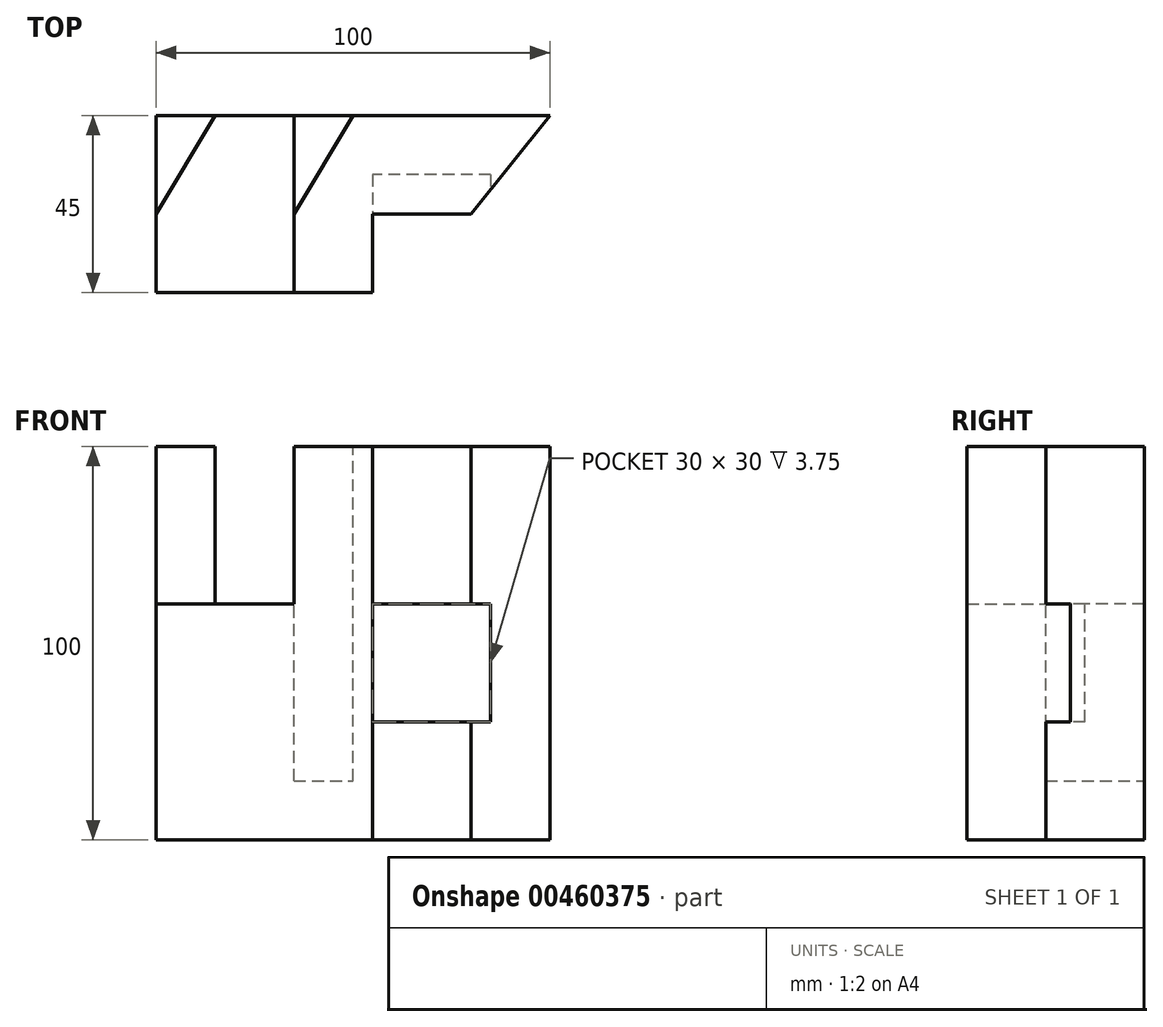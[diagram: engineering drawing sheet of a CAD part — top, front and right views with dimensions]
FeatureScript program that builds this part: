
annotation { "Feature Type Name" : "Feature", "Feature Type Description" : "" }
export const myFeature = defineFeature(function(context is Context, id is Id, definition is map)
    precondition{}
    {
        {
            var Q0;
            Q0=qCreatedBy(makeId("Front.planeOp"),FACE);
            var sketch = newSketch(context, id + "F0", { "sketchPlane" : qUnion([Q0])});
            skLineSegment(sketch, "E0.bottom", {"start": v(0, 0) * mm, "end": v(100, 0) * mm});
            skLineSegment(sketch, "E0.top", {"start": v(0, 100) * mm, "end": v(100, 100) * mm});
            skLineSegment(sketch, "E0.left", {"start": v(0, 0) * mm, "end": v(0, 100) * mm});
            skLineSegment(sketch, "E0.right", {"start": v(100, 0) * mm, "end": v(100, 100) * mm});
            skSolve(sketch);
        }
        {
            var Q0;
            Q0=makeQuery(id+"F0.imprint","IMPRINT",FACE,{"disambiguationData":[TD([[makeQuery(id+"F0.imprint","IMPRINT",EDGE,{"derivedFrom":sQuery(id+"F0.wireOp",EDGE,"E0.bottom")}),1.0]])]});
            extrude(context, id + "F1", {"entities" : qUnion([Q0]), "depth" : 45 * mm});
        }
        {
            var Q0;
            Q0=makeQuery(id+"F1.opExtrude","CAP_FACE",FACE,{"disambiguationData":[OSD([sQuery(id+"F0.wireOp",EDGE,"E0.bottom"),sQuery(id+"F0.wireOp",EDGE,"E0.top"),sQuery(id+"F0.wireOp",EDGE,"E0.left"),sQuery(id+"F0.wireOp",EDGE,"E0.right")])],"isStart":false});
            var sketch = newSketch(context, id + "F2", { "sketchPlane" : qUnion([Q0])});
            skLineSegment(sketch, "E1.bottom", {"start": v(100, 0) * mm, "end": v(55, 0) * mm});
            skLineSegment(sketch, "E1.top", {"start": v(100, 100) * mm, "end": v(55, 100) * mm});
            skLineSegment(sketch, "E1.left", {"start": v(100, 0) * mm, "end": v(100, 100) * mm});
            skLineSegment(sketch, "E1.right", {"start": v(55, 0) * mm, "end": v(55, 100) * mm});
            skSolve(sketch);
        }
        {
            var Q0;
            Q0=makeQuery(id+"F2.imprint","IMPRINT",FACE,{"disambiguationData":[TD([[makeQuery(id+"F2.imprint","IMPRINT",EDGE,{"derivedFrom":sQuery(id+"F2.wireOp",EDGE,"E1.bottom")}),1.0]])]});
            extrude(context, id + "F3", {"entities" : qUnion([Q0]), "operationType" : NewBodyOperationType.REMOVE, "oppositeDirection" : true, "depth" : 20 * mm});
        }
        {
            var Q0;
            Q0=makeQuery(id+"F1.opExtrude","SWEPT_FACE",FACE,{"disambiguationData":[OSD([sQuery(id+"F0.wireOp",EDGE,"E0.top")])]});
            var sketch = newSketch(context, id + "F4", { "sketchPlane" : qUnion([Q0])});
            skLineSegment(sketch, "E2.bottom", {"start": v(0, -45) * mm, "end": v(35, -45) * mm});
            skLineSegment(sketch, "E2.top", {"start": v(0, 0) * mm, "end": v(35, 0) * mm});
            skLineSegment(sketch, "E2.left", {"start": v(0, -45) * mm, "end": v(0, 0) * mm});
            skLineSegment(sketch, "E2.right", {"start": v(35, -45) * mm, "end": v(35, 0) * mm});
            skSolve(sketch);
        }
        {
            var Q0;
            Q0=makeQuery(id+"F4.imprint","IMPRINT",FACE,{"disambiguationData":[TD([[makeQuery(id+"F4.imprint","IMPRINT",EDGE,{"derivedFrom":sQuery(id+"F4.wireOp",EDGE,"E2.bottom")}),1.0]])]});
            extrude(context, id + "F5", {"entities" : qUnion([Q0]), "operationType" : NewBodyOperationType.REMOVE, "oppositeDirection" : true, "depth" : 40 * mm});
        }
        {
            var Q0;
            Q0=makeQuery(id+"F5.boolean.opBoolean","COPY",FACE,{"derivedFrom":makeQuery(id+"F5.opExtrude","CAP_FACE",FACE,{"disambiguationData":[OSD([sQuery(id+"F4.wireOp",EDGE,"E2.bottom"),sQuery(id+"F4.wireOp",EDGE,"E2.top"),sQuery(id+"F4.wireOp",EDGE,"E2.left"),sQuery(id+"F4.wireOp",EDGE,"E2.right")])],"isStart":false})});
            var sketch = newSketch(context, id + "F6", { "sketchPlane" : qUnion([Q0])});
            skLineSegment(sketch, "E3", {"start": v(0, 0) * mm, "end": v(15, 0) * mm});
            skLineSegment(sketch, "E4", {"start": v(15, 0) * mm, "end": v(0, -25) * mm});
            skLineSegment(sketch, "E5", {"start": v(0, -25) * mm, "end": v(0, 0) * mm});
            skSolve(sketch);
        }
        {
            var Q0;
            Q0=makeQuery(id+"F6.imprint","IMPRINT",FACE,{"disambiguationData":[TD([[makeQuery(id+"F6.imprint","IMPRINT",EDGE,{"derivedFrom":sQuery(id+"F6.wireOp",EDGE,"E3")}),-1.0]])]});
            extrude(context, id + "F7", {"entities" : qUnion([Q0]), "operationType" : NewBodyOperationType.ADD, "depth" : 40 * mm});
        }
        {
            var Q0;
            Q0=makeQuery(id+"F3.boolean.opBoolean","COPY",FACE,{"derivedFrom":makeQuery(id+"F3.opExtrude","CAP_FACE",FACE,{"disambiguationData":[OSD([sQuery(id+"F2.wireOp",EDGE,"E1.bottom"),sQuery(id+"F2.wireOp",EDGE,"E1.top"),sQuery(id+"F2.wireOp",EDGE,"E1.left"),sQuery(id+"F2.wireOp",EDGE,"E1.right")])],"isStart":false})});
            var sketch = newSketch(context, id + "F8", { "sketchPlane" : qUnion([Q0])});
            skLineSegment(sketch, "E6", {"start": v(100, 0) * mm, "end": v(85, 0) * mm});
            skLineSegment(sketch, "E7", {"start": v(85, 0) * mm, "end": v(85, 30) * mm});
            skLineSegment(sketch, "E8", {"start": v(85, 30) * mm, "end": v(55, 30) * mm});
            skLineSegment(sketch, "E9", {"start": v(55, 30) * mm, "end": v(55, 60) * mm});
            skLineSegment(sketch, "E10", {"start": v(55, 60) * mm, "end": v(85, 60) * mm});
            skLineSegment(sketch, "E11", {"start": v(85, 60) * mm, "end": v(85, 30) * mm});
            skSolve(sketch);
        }
        {
            var Q0;
            Q0=makeQuery(id+"F1.opExtrude","SWEPT_FACE",FACE,{"disambiguationData":[OSD([sQuery(id+"F0.wireOp",EDGE,"E0.top")])]});
            var sketch = newSketch(context, id + "F9", { "sketchPlane" : qUnion([Q0])});
            skLineSegment(sketch, "E12", {"start": v(100, 0) * mm, "end": v(100, -25) * mm});
            skLineSegment(sketch, "E13", {"start": v(100, -25) * mm, "end": v(80, -25) * mm});
            skLineSegment(sketch, "E14", {"start": v(80, -25) * mm, "end": v(100, 0) * mm});
            skSolve(sketch);
        }
        {
            var Q0;
            Q0=makeQuery(id+"F9.imprint","IMPRINT",FACE,{"disambiguationData":[TD([[makeQuery(id+"F9.imprint","IMPRINT",EDGE,{"derivedFrom":sQuery(id+"F9.wireOp",EDGE,"E12")}),1.0]])]});
            extrude(context, id + "F10", {"entities" : qUnion([Q0]), "operationType" : NewBodyOperationType.REMOVE, "endBound" : BoundingType.THROUGH_ALL, "oppositeDirection" : true, "depth" : 25 * mm});
        }
        {
            var Q0;
            Q0=makeQuery(id+"F8.imprint","IMPRINT",FACE,{"disambiguationData":[TD([[makeQuery(id+"F8.imprint","IMPRINT",EDGE,{"derivedFrom":sQuery(id+"F8.wireOp",EDGE,"E8")}),-1.0]])]});
            extrude(context, id + "F11", {"entities" : qUnion([Q0]), "operationType" : NewBodyOperationType.REMOVE, "oppositeDirection" : true, "depth" : 10 * mm});
        }
        {
            var Q0;
            Q0=makeQuery(id+"F1.opExtrude","SWEPT_FACE",FACE,{"disambiguationData":[OSD([sQuery(id+"F0.wireOp",EDGE,"E0.top")])]});
            var sketch = newSketch(context, id + "F12", { "sketchPlane" : qUnion([Q0])});
            skLineSegment(sketch, "E15", {"start": v(35, 0) * mm, "end": v(35, -25) * mm});
            skLineSegment(sketch, "E16", {"start": v(35, -25) * mm, "end": v(50, 0) * mm});
            skLineSegment(sketch, "E17", {"start": v(35, 0) * mm, "end": v(50, 0) * mm});
            skSolve(sketch);
        }
        {
            var Q0;
            Q0=makeQuery(id+"F12.imprint","IMPRINT",FACE,{"disambiguationData":[TD([[makeQuery(id+"F12.imprint","IMPRINT",EDGE,{"derivedFrom":sQuery(id+"F12.wireOp",EDGE,"E15")}),-1.0]])]});
            extrude(context, id + "F13", {"entities" : qUnion([Q0]), "operationType" : NewBodyOperationType.REMOVE, "oppositeDirection" : true, "depth" : 85 * mm});
        }
    });
